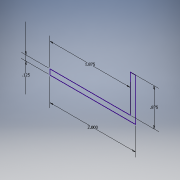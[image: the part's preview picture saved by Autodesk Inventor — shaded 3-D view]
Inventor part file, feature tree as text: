
AUTODESK INVENTOR PART (.ipt)
format: ipt  version: 2016 (Build 200138000, 138)  size: 114,176 bytes
history: native  units: in
note: dims shown in document units (in); Inventor stores cm internally (conversion verified against a paired STEP export)
features: other x3, sketch x3
ambient origin geometry x8: Origin, YZ Plane, XZ Plane, XY Plane, X Axis, Y Axis, Z Axis, Center Point
bodies: Solid1 (feature_tree)
feature tree (6):
  other  "rail gusset .ipt"
  other  "Solid1::rail gusset .ipt"
  other  "TaggingFeature1"
  sketch  "Sketch1"  dims[d0=0.3937in]
  sketch  "Sketch2"
  sketch  "Sketch3"
